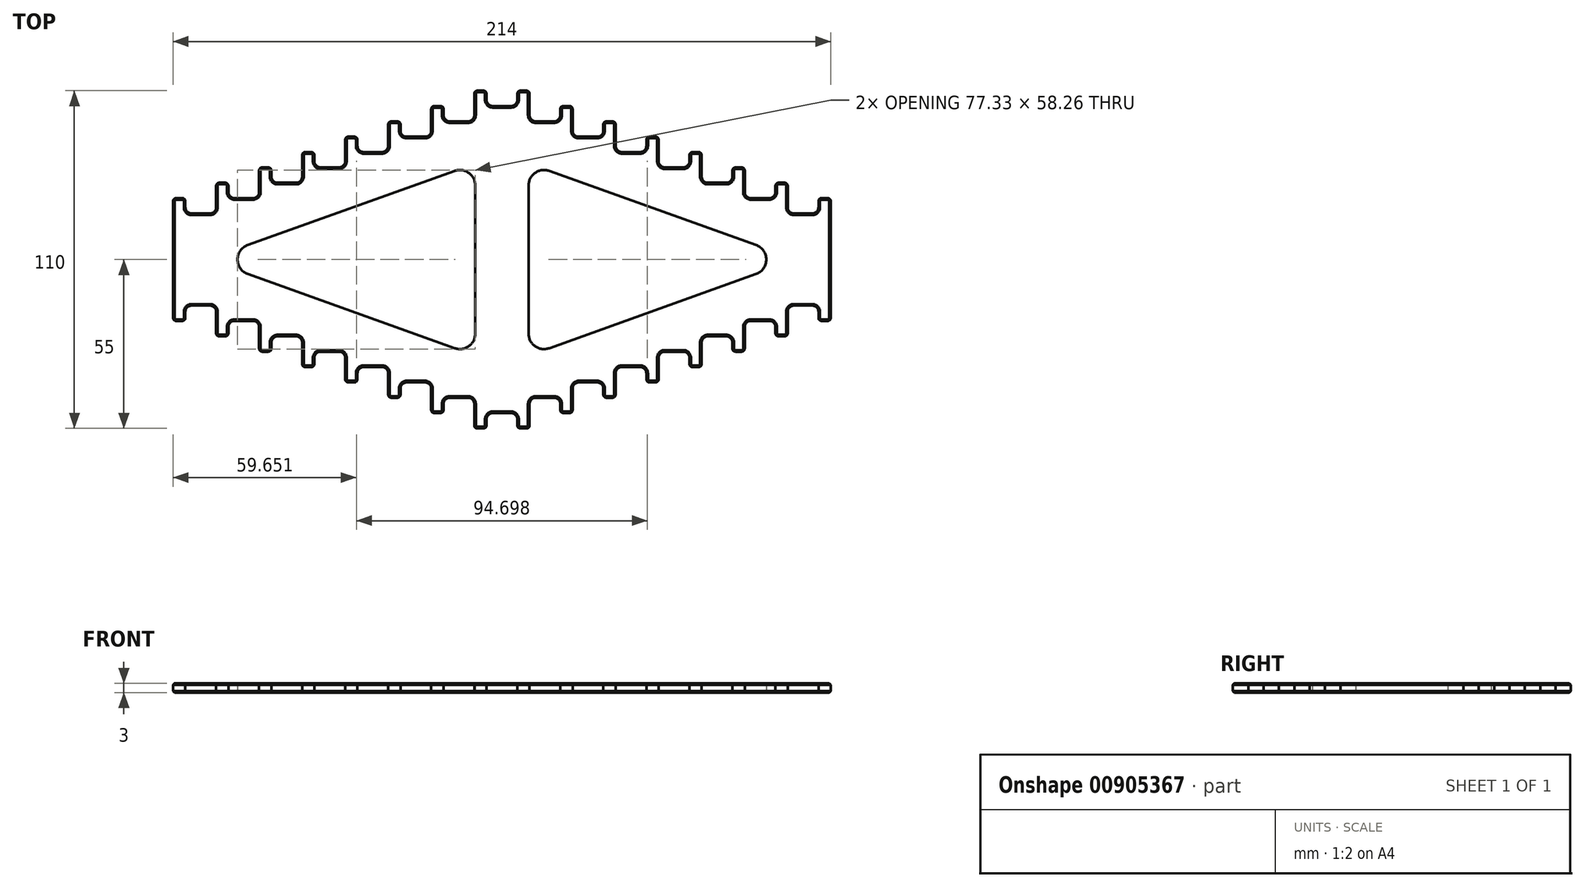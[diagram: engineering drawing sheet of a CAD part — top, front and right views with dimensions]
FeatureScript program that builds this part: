
annotation { "Feature Type Name" : "Feature", "Feature Type Description" : "" }
export const myFeature = defineFeature(function(context is Context, id is Id, definition is map)
    precondition{}
    {
        {
            var Q0;
            Q0=qCreatedBy(makeId("Top.planeOp"),FACE);
            var sketch = newSketch(context, id + "F0", { "sketchPlane" : qUnion([Q0])});
            skLineSegment(sketch, "E0", {"start": v(0, 0) * mm, "end": v(0, 34.38) * mm, "construction": true});
            skLineSegment(sketch, "E1", {"start": v(0, 0) * mm, "end": v(-95.82, 0) * mm, "construction": true});
            skLineSegment(sketch, "E2", {"start": v(0, 50) * mm, "end": v(-5, 50) * mm});
            skLineSegment(sketch, "E3", {"start": v(-5, 50) * mm, "end": v(-5, 55) * mm});
            skLineSegment(sketch, "E4", {"start": v(-5, 55) * mm, "end": v(-9, 55) * mm});
            skLineSegment(sketch, "E5", {"start": v(-9, 55) * mm, "end": v(-9, 45) * mm});
            skLineSegment(sketch, "E6", {"start": v(-9, 45) * mm, "end": v(-19, 45) * mm});
            skLineSegment(sketch, "E7", {"start": v(-19, 45) * mm, "end": v(-19, 50) * mm});
            skLineSegment(sketch, "E8", {"start": v(-19, 50) * mm, "end": v(-23, 50) * mm});
            skLineSegment(sketch, "E9", {"start": v(-23, 50) * mm, "end": v(-23, 40) * mm});
            skLineSegment(sketch, "E10", {"start": v(-23, 40) * mm, "end": v(-33, 40) * mm});
            skLineSegment(sketch, "E11", {"start": v(-33, 40) * mm, "end": v(-33, 45) * mm});
            skLineSegment(sketch, "E12", {"start": v(-33, 45) * mm, "end": v(-37, 45) * mm});
            skLineSegment(sketch, "E13", {"start": v(-37, 45) * mm, "end": v(-37, 35) * mm});
            skLineSegment(sketch, "E14", {"start": v(-37, 35) * mm, "end": v(-47, 35) * mm});
            skLineSegment(sketch, "E15", {"start": v(-47, 35) * mm, "end": v(-47, 40) * mm});
            skLineSegment(sketch, "E16", {"start": v(-47, 40) * mm, "end": v(-51, 40) * mm});
            skLineSegment(sketch, "E17", {"start": v(-51, 40) * mm, "end": v(-51, 30) * mm});
            skLineSegment(sketch, "E18", {"start": v(-51, 30) * mm, "end": v(-61, 30) * mm});
            skLineSegment(sketch, "E19", {"start": v(-61, 30) * mm, "end": v(-61, 35) * mm});
            skLineSegment(sketch, "E20", {"start": v(-61, 35) * mm, "end": v(-65, 35) * mm});
            skLineSegment(sketch, "E21", {"start": v(-65, 35) * mm, "end": v(-65, 25) * mm});
            skLineSegment(sketch, "E22", {"start": v(-65, 25) * mm, "end": v(-75, 25) * mm});
            skLineSegment(sketch, "E23", {"start": v(-75, 25) * mm, "end": v(-75, 30) * mm});
            skLineSegment(sketch, "E24", {"start": v(-75, 30) * mm, "end": v(-79, 30) * mm});
            skLineSegment(sketch, "E25", {"start": v(-79, 30) * mm, "end": v(-79, 20) * mm});
            skLineSegment(sketch, "E26", {"start": v(-79, 20) * mm, "end": v(-89, 20) * mm});
            skLineSegment(sketch, "E27", {"start": v(-89, 20) * mm, "end": v(-89, 25) * mm});
            skLineSegment(sketch, "E28", {"start": v(-89, 25) * mm, "end": v(-93, 25) * mm});
            skLineSegment(sketch, "E29", {"start": v(-93, 25) * mm, "end": v(-93, 15) * mm});
            skLineSegment(sketch, "E30", {"start": v(-93, 15) * mm, "end": v(-103, 15) * mm});
            skLineSegment(sketch, "E31", {"start": v(-103, 15) * mm, "end": v(-103, 20) * mm});
            skLineSegment(sketch, "E32", {"start": v(-103, 20) * mm, "end": v(-107, 20) * mm});
            skLineSegment(sketch, "E33", {"start": v(-107, 20) * mm, "end": v(-107, 0) * mm});
            skLineSegment(sketch, "E34.MirrorCS", {"start": v(47, 40) * mm, "end": v(51, 40) * mm});
            skLineSegment(sketch, "E35.MirrorCS", {"start": v(75, 30) * mm, "end": v(79, 30) * mm});
            skLineSegment(sketch, "E36.MirrorCS", {"start": v(61, 35) * mm, "end": v(65, 35) * mm});
            skLineSegment(sketch, "E37.MirrorCS", {"start": v(33, 45) * mm, "end": v(37, 45) * mm});
            skLineSegment(sketch, "E38.MirrorCS", {"start": v(89, 20) * mm, "end": v(89, 25) * mm});
            skLineSegment(sketch, "E39.MirrorCS", {"start": v(51, 30) * mm, "end": v(61, 30) * mm});
            skLineSegment(sketch, "E40.MirrorCS", {"start": v(37, 45) * mm, "end": v(37, 35) * mm});
            skLineSegment(sketch, "E41.MirrorCS", {"start": v(19, 45) * mm, "end": v(19, 50) * mm});
            skLineSegment(sketch, "E42.MirrorCS", {"start": v(65, 25) * mm, "end": v(75, 25) * mm});
            skLineSegment(sketch, "E43.MirrorCS", {"start": v(9, 45) * mm, "end": v(19, 45) * mm});
            skLineSegment(sketch, "E44.MirrorCS", {"start": v(79, 30) * mm, "end": v(79, 20) * mm});
            skLineSegment(sketch, "E45.MirrorCS", {"start": v(75, 25) * mm, "end": v(75, 30) * mm});
            skLineSegment(sketch, "E46.MirrorCS", {"start": v(65, 35) * mm, "end": v(65, 25) * mm});
            skLineSegment(sketch, "E47.MirrorCS", {"start": v(5, 50) * mm, "end": v(5, 55) * mm});
            skLineSegment(sketch, "E48.MirrorCS", {"start": v(47, 35) * mm, "end": v(47, 40) * mm});
            skLineSegment(sketch, "E49.MirrorCS", {"start": v(61, 30) * mm, "end": v(61, 35) * mm});
            skLineSegment(sketch, "E50.MirrorCS", {"start": v(103, 20) * mm, "end": v(107, 20) * mm});
            skLineSegment(sketch, "E51.MirrorCS", {"start": v(79, 20) * mm, "end": v(89, 20) * mm});
            skLineSegment(sketch, "E52.MirrorCS", {"start": v(89, 25) * mm, "end": v(93, 25) * mm});
            skLineSegment(sketch, "E53.MirrorCS", {"start": v(103, 15) * mm, "end": v(103, 20) * mm});
            skLineSegment(sketch, "E54.MirrorCS", {"start": v(9, 55) * mm, "end": v(9, 45) * mm});
            skLineSegment(sketch, "E55.MirrorCS", {"start": v(37, 35) * mm, "end": v(47, 35) * mm});
            skLineSegment(sketch, "E56.MirrorCS", {"start": v(51, 40) * mm, "end": v(51, 30) * mm});
            skLineSegment(sketch, "E57.MirrorCS", {"start": v(93, 25) * mm, "end": v(93, 15) * mm});
            skLineSegment(sketch, "E58.MirrorCS", {"start": v(33, 40) * mm, "end": v(33, 45) * mm});
            skLineSegment(sketch, "E59.MirrorCS", {"start": v(23, 50) * mm, "end": v(23, 40) * mm});
            skLineSegment(sketch, "E60.MirrorCS", {"start": v(93, 15) * mm, "end": v(103, 15) * mm});
            skLineSegment(sketch, "E61.MirrorCS", {"start": v(19, 50) * mm, "end": v(23, 50) * mm});
            skLineSegment(sketch, "E62.MirrorCS", {"start": v(23, 40) * mm, "end": v(33, 40) * mm});
            skLineSegment(sketch, "E63.MirrorCS", {"start": v(5, 55) * mm, "end": v(9, 55) * mm});
            skLineSegment(sketch, "E64.MirrorCS", {"start": v(107, 20) * mm, "end": v(107, 0) * mm});
            skLineSegment(sketch, "E65.MirrorCS", {"start": v(-33, -45) * mm, "end": v(-37, -45) * mm});
            skLineSegment(sketch, "E66.MirrorCS", {"start": v(-33, -40) * mm, "end": v(-33, -45) * mm});
            skLineSegment(sketch, "E67.MirrorCS", {"start": v(33, -40) * mm, "end": v(33, -45) * mm});
            skLineSegment(sketch, "E68.MirrorCS", {"start": v(-61, -30) * mm, "end": v(-61, -35) * mm});
            skLineSegment(sketch, "E69.MirrorCS", {"start": v(-47, -35) * mm, "end": v(-47, -40) * mm});
            skLineSegment(sketch, "E70.MirrorCS", {"start": v(5, -55) * mm, "end": v(9, -55) * mm});
            skLineSegment(sketch, "E71.MirrorCS", {"start": v(-75, -30) * mm, "end": v(-79, -30) * mm});
            skLineSegment(sketch, "E72.MirrorCS", {"start": v(-89, -20) * mm, "end": v(-89, -25) * mm});
            skLineSegment(sketch, "E73.MirrorCS", {"start": v(103, -15) * mm, "end": v(103, -20) * mm});
            skLineSegment(sketch, "E74.MirrorCS", {"start": v(-19, -45) * mm, "end": v(-19, -50) * mm});
            skLineSegment(sketch, "E75.MirrorCS", {"start": v(-103, -20) * mm, "end": v(-107, -20) * mm});
            skLineSegment(sketch, "E76.MirrorCS", {"start": v(75, -30) * mm, "end": v(79, -30) * mm});
            skLineSegment(sketch, "E77.MirrorCS", {"start": v(-89, -25) * mm, "end": v(-93, -25) * mm});
            skLineSegment(sketch, "E78.MirrorCS", {"start": v(-47, -40) * mm, "end": v(-51, -40) * mm});
            skLineSegment(sketch, "E79.MirrorCS", {"start": v(89, -20) * mm, "end": v(89, -25) * mm});
            skLineSegment(sketch, "E80.MirrorCS", {"start": v(103, -20) * mm, "end": v(107, -20) * mm});
            skLineSegment(sketch, "E81.MirrorCS", {"start": v(19, -45) * mm, "end": v(19, -50) * mm});
            skLineSegment(sketch, "E82.MirrorCS", {"start": v(61, -30) * mm, "end": v(61, -35) * mm});
            skLineSegment(sketch, "E83.MirrorCS", {"start": v(-103, -15) * mm, "end": v(-103, -20) * mm});
            skLineSegment(sketch, "E84.MirrorCS", {"start": v(-5, -50) * mm, "end": v(-5, -55) * mm});
            skLineSegment(sketch, "E85.MirrorCS", {"start": v(47, -40) * mm, "end": v(51, -40) * mm});
            skLineSegment(sketch, "E86.MirrorCS", {"start": v(19, -50) * mm, "end": v(23, -50) * mm});
            skLineSegment(sketch, "E87.MirrorCS", {"start": v(-5, -55) * mm, "end": v(-9, -55) * mm});
            skLineSegment(sketch, "E88.MirrorCS", {"start": v(-61, -35) * mm, "end": v(-65, -35) * mm});
            skLineSegment(sketch, "E89.MirrorCS", {"start": v(89, -25) * mm, "end": v(93, -25) * mm});
            skLineSegment(sketch, "E90.MirrorCS", {"start": v(33, -45) * mm, "end": v(37, -45) * mm});
            skLineSegment(sketch, "E91.MirrorCS", {"start": v(47, -35) * mm, "end": v(47, -40) * mm});
            skLineSegment(sketch, "E92.MirrorCS", {"start": v(75, -25) * mm, "end": v(75, -30) * mm});
            skLineSegment(sketch, "E93.MirrorCS", {"start": v(-19, -50) * mm, "end": v(-23, -50) * mm});
            skLineSegment(sketch, "E94.MirrorCS", {"start": v(61, -35) * mm, "end": v(65, -35) * mm});
            skLineSegment(sketch, "E95.MirrorCS", {"start": v(-75, -25) * mm, "end": v(-75, -30) * mm});
            skLineSegment(sketch, "E96.MirrorCS", {"start": v(0, -50) * mm, "end": v(-5, -50) * mm});
            skLineSegment(sketch, "E97.MirrorCS", {"start": v(5, -50) * mm, "end": v(5, -55) * mm});
            skLineSegment(sketch, "E98.MirrorCS", {"start": v(65, -35) * mm, "end": v(65, -25) * mm});
            skLineSegment(sketch, "E99.MirrorCS", {"start": v(-93, -15) * mm, "end": v(-103, -15) * mm});
            skLineSegment(sketch, "E100.MirrorCS", {"start": v(-37, -45) * mm, "end": v(-37, -35) * mm});
            skLineSegment(sketch, "E101.MirrorCS", {"start": v(-93, -25) * mm, "end": v(-93, -15) * mm});
            skLineSegment(sketch, "E102.MirrorCS", {"start": v(-51, -30) * mm, "end": v(-61, -30) * mm});
            skLineSegment(sketch, "E103.MirrorCS", {"start": v(79, -20) * mm, "end": v(89, -20) * mm});
            skLineSegment(sketch, "E104.MirrorCS", {"start": v(-51, -40) * mm, "end": v(-51, -30) * mm});
            skLineSegment(sketch, "E105.MirrorCS", {"start": v(-23, -40) * mm, "end": v(-33, -40) * mm});
            skLineSegment(sketch, "E106.MirrorCS", {"start": v(37, -35) * mm, "end": v(47, -35) * mm});
            skLineSegment(sketch, "E107.MirrorCS", {"start": v(79, -30) * mm, "end": v(79, -20) * mm});
            skLineSegment(sketch, "E108.MirrorCS", {"start": v(-9, -45) * mm, "end": v(-19, -45) * mm});
            skLineSegment(sketch, "E109.MirrorCS", {"start": v(51, -30) * mm, "end": v(61, -30) * mm});
            skLineSegment(sketch, "E110.MirrorCS", {"start": v(-65, -35) * mm, "end": v(-65, -25) * mm});
            skLineSegment(sketch, "E111.MirrorCS", {"start": v(-23, -50) * mm, "end": v(-23, -40) * mm});
            skLineSegment(sketch, "E112.MirrorCS", {"start": v(93, -25) * mm, "end": v(93, -15) * mm});
            skLineSegment(sketch, "E113.MirrorCS", {"start": v(9, -45) * mm, "end": v(19, -45) * mm});
            skLineSegment(sketch, "E114.MirrorCS", {"start": v(-9, -55) * mm, "end": v(-9, -45) * mm});
            skLineSegment(sketch, "E115.MirrorCS", {"start": v(23, -40) * mm, "end": v(33, -40) * mm});
            skLineSegment(sketch, "E116.MirrorCS", {"start": v(-79, -30) * mm, "end": v(-79, -20) * mm});
            skLineSegment(sketch, "E117.MirrorCS", {"start": v(9, -55) * mm, "end": v(9, -45) * mm});
            skLineSegment(sketch, "E118.MirrorCS", {"start": v(-79, -20) * mm, "end": v(-89, -20) * mm});
            skLineSegment(sketch, "E119.MirrorCS", {"start": v(23, -50) * mm, "end": v(23, -40) * mm});
            skLineSegment(sketch, "E120.MirrorCS", {"start": v(51, -40) * mm, "end": v(51, -30) * mm});
            skLineSegment(sketch, "E121.MirrorCS", {"start": v(37, -45) * mm, "end": v(37, -35) * mm});
            skLineSegment(sketch, "E122.MirrorCS", {"start": v(-65, -25) * mm, "end": v(-75, -25) * mm});
            skLineSegment(sketch, "E123.MirrorCS", {"start": v(-37, -35) * mm, "end": v(-47, -35) * mm});
            skLineSegment(sketch, "E124.MirrorCS", {"start": v(93, -15) * mm, "end": v(103, -15) * mm});
            skLineSegment(sketch, "E125.MirrorCS", {"start": v(65, -25) * mm, "end": v(75, -25) * mm});
            skLineSegment(sketch, "E126.MirrorCS", {"start": v(107, -20) * mm, "end": v(107, 0) * mm});
            skLineSegment(sketch, "E127.MirrorCS", {"start": v(-107, -20) * mm, "end": v(-107, 0) * mm});
            skLineSegment(sketch, "E128", {"start": v(5, 50) * mm, "end": v(0, 50) * mm});
            skLineSegment(sketch, "E129", {"start": v(5, -50) * mm, "end": v(0, -50) * mm});
            skLineSegment(sketch, "E130.MirrorCS", {"start": v(0, 0) * mm, "end": v(0, -34.38) * mm, "construction": true});
            skLineSegment(sketch, "E131.MirrorCS", {"start": v(0, 0) * mm, "end": v(95.82, 0) * mm, "construction": true});
            skLineSegment(sketch, "E132", {"start": v(-95.82, 0) * mm, "end": v(0, 34.38) * mm});
            skLineSegment(sketch, "E133.MirrorCS", {"start": v(95.82, 0) * mm, "end": v(0, 34.38) * mm});
            skLineSegment(sketch, "E134.MirrorCS", {"start": v(-95.82, 0) * mm, "end": v(0, -34.38) * mm});
            skLineSegment(sketch, "E135.MirrorCS", {"start": v(95.82, 0) * mm, "end": v(0, -34.38) * mm});
            skLineSegment(sketch, "E136", {"start": v(-8.68, 31.26) * mm, "end": v(-8.68, -31.26) * mm});
            skLineSegment(sketch, "E137.MirrorCS", {"start": v(8.68, 31.26) * mm, "end": v(8.68, -31.26) * mm});
            skSolve(sketch);
        }
        {
            var Q0;
            Q0=makeQuery(id+"F0.imprint","IMPRINT",FACE,{"disambiguationData":[TD([[makeQuery(id+"F0.imprint","IMPRINT",EDGE,{"derivedFrom":sQuery(id+"F0.wireOp",EDGE,"E2")}),1.0]])]});
            var Q1;
            {var subQ4=sQuery(id+"F0.wireOp",EDGE,"E136");Q1=makeQuery(id+"F0.imprint","IMPRINT",FACE,{"disambiguationData":[TD([[makeQuery(id+"F0.imprint","IMPRINT",EDGE,{"derivedFrom":subQ4}),1.0]])]});}
            extrude(context, id + "F1", {"entities" : qUnion([Q0, Q1]), "depth" : 3 * mm, "offsetDistance" : 25 * mm});
        }
        {
            var Q0;
            Q0=makeQuery(id+"F1.opExtrude","SWEPT_EDGE",EDGE,{"disambiguationData":[OSD([sQuery(id+"F0.wireOp",EDGE,"E30"),sQuery(id+"F0.wireOp",EDGE,"E31")])]});
            var Q1;
            Q1=makeQuery(id+"F1.opExtrude","SWEPT_EDGE",EDGE,{"disambiguationData":[OSD([sQuery(id+"F0.wireOp",EDGE,"E26"),sQuery(id+"F0.wireOp",EDGE,"E27")])]});
            var Q2;
            Q2=makeQuery(id+"F1.opExtrude","SWEPT_EDGE",EDGE,{"disambiguationData":[OSD([sQuery(id+"F0.wireOp",EDGE,"E22"),sQuery(id+"F0.wireOp",EDGE,"E23")])]});
            var Q3;
            Q3=makeQuery(id+"F1.opExtrude","SWEPT_EDGE",EDGE,{"disambiguationData":[OSD([sQuery(id+"F0.wireOp",EDGE,"E18"),sQuery(id+"F0.wireOp",EDGE,"E19")])]});
            var Q4;
            Q4=makeQuery(id+"F1.opExtrude","SWEPT_EDGE",EDGE,{"disambiguationData":[OSD([sQuery(id+"F0.wireOp",EDGE,"E14"),sQuery(id+"F0.wireOp",EDGE,"E15")])]});
            var Q5;
            Q5=makeQuery(id+"F1.opExtrude","SWEPT_EDGE",EDGE,{"disambiguationData":[OSD([sQuery(id+"F0.wireOp",EDGE,"E10"),sQuery(id+"F0.wireOp",EDGE,"E11")])]});
            var Q6;
            Q6=makeQuery(id+"F1.opExtrude","SWEPT_EDGE",EDGE,{"disambiguationData":[OSD([sQuery(id+"F0.wireOp",EDGE,"E6"),sQuery(id+"F0.wireOp",EDGE,"E7")])]});
            var Q7;
            Q7=makeQuery(id+"F1.opExtrude","SWEPT_EDGE",EDGE,{"disambiguationData":[OSD([sQuery(id+"F0.wireOp",EDGE,"E2"),sQuery(id+"F0.wireOp",EDGE,"E3")])]});
            var Q8;
            Q8=makeQuery(id+"F1.opExtrude","SWEPT_EDGE",EDGE,{"disambiguationData":[OSD([sQuery(id+"F0.wireOp",EDGE,"E29"),sQuery(id+"F0.wireOp",EDGE,"E30")])]});
            var Q9;
            Q9=makeQuery(id+"F1.opExtrude","SWEPT_EDGE",EDGE,{"disambiguationData":[OSD([sQuery(id+"F0.wireOp",EDGE,"E25"),sQuery(id+"F0.wireOp",EDGE,"E26")])]});
            var Q10;
            Q10=makeQuery(id+"F1.opExtrude","SWEPT_EDGE",EDGE,{"disambiguationData":[OSD([sQuery(id+"F0.wireOp",EDGE,"E21"),sQuery(id+"F0.wireOp",EDGE,"E22")])]});
            var Q11;
            Q11=makeQuery(id+"F1.opExtrude","SWEPT_EDGE",EDGE,{"disambiguationData":[OSD([sQuery(id+"F0.wireOp",EDGE,"E17"),sQuery(id+"F0.wireOp",EDGE,"E18")])]});
            var Q12;
            Q12=makeQuery(id+"F1.opExtrude","SWEPT_EDGE",EDGE,{"disambiguationData":[OSD([sQuery(id+"F0.wireOp",EDGE,"E13"),sQuery(id+"F0.wireOp",EDGE,"E14")])]});
            var Q13;
            Q13=makeQuery(id+"F1.opExtrude","SWEPT_EDGE",EDGE,{"disambiguationData":[OSD([sQuery(id+"F0.wireOp",EDGE,"E9"),sQuery(id+"F0.wireOp",EDGE,"E10")])]});
            var Q14;
            Q14=makeQuery(id+"F1.opExtrude","SWEPT_EDGE",EDGE,{"disambiguationData":[OSD([sQuery(id+"F0.wireOp",EDGE,"E5"),sQuery(id+"F0.wireOp",EDGE,"E6")])]});
            var Q15;
            Q15=makeQuery(id+"F1.opExtrude","SWEPT_EDGE",EDGE,{"disambiguationData":[OSD([sQuery(id+"F0.wireOp",EDGE,"E47.MirrorCS"),sQuery(id+"F0.wireOp",EDGE,"E128")])]});
            var Q16;
            Q16=makeQuery(id+"F1.opExtrude","SWEPT_EDGE",EDGE,{"disambiguationData":[OSD([sQuery(id+"F0.wireOp",EDGE,"E41.MirrorCS"),sQuery(id+"F0.wireOp",EDGE,"E43.MirrorCS")])]});
            var Q17;
            Q17=makeQuery(id+"F1.opExtrude","SWEPT_EDGE",EDGE,{"disambiguationData":[OSD([sQuery(id+"F0.wireOp",EDGE,"E58.MirrorCS"),sQuery(id+"F0.wireOp",EDGE,"E62.MirrorCS")])]});
            var Q18;
            Q18=makeQuery(id+"F1.opExtrude","SWEPT_EDGE",EDGE,{"disambiguationData":[OSD([sQuery(id+"F0.wireOp",EDGE,"E48.MirrorCS"),sQuery(id+"F0.wireOp",EDGE,"E55.MirrorCS")])]});
            var Q19;
            Q19=makeQuery(id+"F1.opExtrude","SWEPT_EDGE",EDGE,{"disambiguationData":[OSD([sQuery(id+"F0.wireOp",EDGE,"E39.MirrorCS"),sQuery(id+"F0.wireOp",EDGE,"E49.MirrorCS")])]});
            var Q20;
            Q20=makeQuery(id+"F1.opExtrude","SWEPT_EDGE",EDGE,{"disambiguationData":[OSD([sQuery(id+"F0.wireOp",EDGE,"E42.MirrorCS"),sQuery(id+"F0.wireOp",EDGE,"E45.MirrorCS")])]});
            var Q21;
            Q21=makeQuery(id+"F1.opExtrude","SWEPT_EDGE",EDGE,{"disambiguationData":[OSD([sQuery(id+"F0.wireOp",EDGE,"E38.MirrorCS"),sQuery(id+"F0.wireOp",EDGE,"E51.MirrorCS")])]});
            var Q22;
            Q22=makeQuery(id+"F1.opExtrude","SWEPT_EDGE",EDGE,{"disambiguationData":[OSD([sQuery(id+"F0.wireOp",EDGE,"E53.MirrorCS"),sQuery(id+"F0.wireOp",EDGE,"E60.MirrorCS")])]});
            var Q23;
            Q23=makeQuery(id+"F1.opExtrude","SWEPT_EDGE",EDGE,{"disambiguationData":[OSD([sQuery(id+"F0.wireOp",EDGE,"E43.MirrorCS"),sQuery(id+"F0.wireOp",EDGE,"E54.MirrorCS")])]});
            var Q24;
            Q24=makeQuery(id+"F1.opExtrude","SWEPT_EDGE",EDGE,{"disambiguationData":[OSD([sQuery(id+"F0.wireOp",EDGE,"E59.MirrorCS"),sQuery(id+"F0.wireOp",EDGE,"E62.MirrorCS")])]});
            var Q25;
            Q25=makeQuery(id+"F1.opExtrude","SWEPT_EDGE",EDGE,{"disambiguationData":[OSD([sQuery(id+"F0.wireOp",EDGE,"E40.MirrorCS"),sQuery(id+"F0.wireOp",EDGE,"E55.MirrorCS")])]});
            var Q26;
            Q26=makeQuery(id+"F1.opExtrude","SWEPT_EDGE",EDGE,{"disambiguationData":[OSD([sQuery(id+"F0.wireOp",EDGE,"E39.MirrorCS"),sQuery(id+"F0.wireOp",EDGE,"E56.MirrorCS")])]});
            var Q27;
            Q27=makeQuery(id+"F1.opExtrude","SWEPT_EDGE",EDGE,{"disambiguationData":[OSD([sQuery(id+"F0.wireOp",EDGE,"E42.MirrorCS"),sQuery(id+"F0.wireOp",EDGE,"E46.MirrorCS")])]});
            var Q28;
            Q28=makeQuery(id+"F1.opExtrude","SWEPT_EDGE",EDGE,{"disambiguationData":[OSD([sQuery(id+"F0.wireOp",EDGE,"E44.MirrorCS"),sQuery(id+"F0.wireOp",EDGE,"E51.MirrorCS")])]});
            var Q29;
            Q29=makeQuery(id+"F1.opExtrude","SWEPT_EDGE",EDGE,{"disambiguationData":[OSD([sQuery(id+"F0.wireOp",EDGE,"E57.MirrorCS"),sQuery(id+"F0.wireOp",EDGE,"E60.MirrorCS")])]});
            var Q30;
            Q30=makeQuery(id+"F1.opExtrude","SWEPT_EDGE",EDGE,{"disambiguationData":[OSD([sQuery(id+"F0.wireOp",EDGE,"E112.MirrorCS"),sQuery(id+"F0.wireOp",EDGE,"E124.MirrorCS")])]});
            var Q31;
            Q31=makeQuery(id+"F1.opExtrude","SWEPT_EDGE",EDGE,{"disambiguationData":[OSD([sQuery(id+"F0.wireOp",EDGE,"E103.MirrorCS"),sQuery(id+"F0.wireOp",EDGE,"E107.MirrorCS")])]});
            var Q32;
            Q32=makeQuery(id+"F1.opExtrude","SWEPT_EDGE",EDGE,{"disambiguationData":[OSD([sQuery(id+"F0.wireOp",EDGE,"E98.MirrorCS"),sQuery(id+"F0.wireOp",EDGE,"E125.MirrorCS")])]});
            var Q33;
            Q33=makeQuery(id+"F1.opExtrude","SWEPT_EDGE",EDGE,{"disambiguationData":[OSD([sQuery(id+"F0.wireOp",EDGE,"E109.MirrorCS"),sQuery(id+"F0.wireOp",EDGE,"E120.MirrorCS")])]});
            var Q34;
            Q34=makeQuery(id+"F1.opExtrude","SWEPT_EDGE",EDGE,{"disambiguationData":[OSD([sQuery(id+"F0.wireOp",EDGE,"E106.MirrorCS"),sQuery(id+"F0.wireOp",EDGE,"E121.MirrorCS")])]});
            var Q35;
            Q35=makeQuery(id+"F1.opExtrude","SWEPT_EDGE",EDGE,{"disambiguationData":[OSD([sQuery(id+"F0.wireOp",EDGE,"E115.MirrorCS"),sQuery(id+"F0.wireOp",EDGE,"E119.MirrorCS")])]});
            var Q36;
            Q36=makeQuery(id+"F1.opExtrude","SWEPT_EDGE",EDGE,{"disambiguationData":[OSD([sQuery(id+"F0.wireOp",EDGE,"E113.MirrorCS"),sQuery(id+"F0.wireOp",EDGE,"E117.MirrorCS")])]});
            var Q37;
            Q37=makeQuery(id+"F1.opExtrude","SWEPT_EDGE",EDGE,{"disambiguationData":[OSD([sQuery(id+"F0.wireOp",EDGE,"E84.MirrorCS"),sQuery(id+"F0.wireOp",EDGE,"E96.MirrorCS")])]});
            var Q38;
            Q38=makeQuery(id+"F1.opExtrude","SWEPT_EDGE",EDGE,{"disambiguationData":[OSD([sQuery(id+"F0.wireOp",EDGE,"E74.MirrorCS"),sQuery(id+"F0.wireOp",EDGE,"E108.MirrorCS")])]});
            var Q39;
            Q39=makeQuery(id+"F1.opExtrude","SWEPT_EDGE",EDGE,{"disambiguationData":[OSD([sQuery(id+"F0.wireOp",EDGE,"E66.MirrorCS"),sQuery(id+"F0.wireOp",EDGE,"E105.MirrorCS")])]});
            var Q40;
            Q40=makeQuery(id+"F1.opExtrude","SWEPT_EDGE",EDGE,{"disambiguationData":[OSD([sQuery(id+"F0.wireOp",EDGE,"E69.MirrorCS"),sQuery(id+"F0.wireOp",EDGE,"E123.MirrorCS")])]});
            var Q41;
            Q41=makeQuery(id+"F1.opExtrude","SWEPT_EDGE",EDGE,{"disambiguationData":[OSD([sQuery(id+"F0.wireOp",EDGE,"E68.MirrorCS"),sQuery(id+"F0.wireOp",EDGE,"E102.MirrorCS")])]});
            var Q42;
            Q42=makeQuery(id+"F1.opExtrude","SWEPT_EDGE",EDGE,{"disambiguationData":[OSD([sQuery(id+"F0.wireOp",EDGE,"E95.MirrorCS"),sQuery(id+"F0.wireOp",EDGE,"E122.MirrorCS")])]});
            var Q43;
            Q43=makeQuery(id+"F1.opExtrude","SWEPT_EDGE",EDGE,{"disambiguationData":[OSD([sQuery(id+"F0.wireOp",EDGE,"E72.MirrorCS"),sQuery(id+"F0.wireOp",EDGE,"E118.MirrorCS")])]});
            var Q44;
            Q44=makeQuery(id+"F1.opExtrude","SWEPT_EDGE",EDGE,{"disambiguationData":[OSD([sQuery(id+"F0.wireOp",EDGE,"E83.MirrorCS"),sQuery(id+"F0.wireOp",EDGE,"E99.MirrorCS")])]});
            var Q45;
            Q45=makeQuery(id+"F1.opExtrude","SWEPT_EDGE",EDGE,{"disambiguationData":[OSD([sQuery(id+"F0.wireOp",EDGE,"E99.MirrorCS"),sQuery(id+"F0.wireOp",EDGE,"E101.MirrorCS")])]});
            var Q46;
            Q46=makeQuery(id+"F1.opExtrude","SWEPT_EDGE",EDGE,{"disambiguationData":[OSD([sQuery(id+"F0.wireOp",EDGE,"E116.MirrorCS"),sQuery(id+"F0.wireOp",EDGE,"E118.MirrorCS")])]});
            var Q47;
            Q47=makeQuery(id+"F1.opExtrude","SWEPT_EDGE",EDGE,{"disambiguationData":[OSD([sQuery(id+"F0.wireOp",EDGE,"E110.MirrorCS"),sQuery(id+"F0.wireOp",EDGE,"E122.MirrorCS")])]});
            var Q48;
            Q48=makeQuery(id+"F1.opExtrude","SWEPT_EDGE",EDGE,{"disambiguationData":[OSD([sQuery(id+"F0.wireOp",EDGE,"E102.MirrorCS"),sQuery(id+"F0.wireOp",EDGE,"E104.MirrorCS")])]});
            var Q49;
            Q49=makeQuery(id+"F1.opExtrude","SWEPT_EDGE",EDGE,{"disambiguationData":[OSD([sQuery(id+"F0.wireOp",EDGE,"E100.MirrorCS"),sQuery(id+"F0.wireOp",EDGE,"E123.MirrorCS")])]});
            var Q50;
            Q50=makeQuery(id+"F1.opExtrude","SWEPT_EDGE",EDGE,{"disambiguationData":[OSD([sQuery(id+"F0.wireOp",EDGE,"E105.MirrorCS"),sQuery(id+"F0.wireOp",EDGE,"E111.MirrorCS")])]});
            var Q51;
            Q51=makeQuery(id+"F1.opExtrude","SWEPT_EDGE",EDGE,{"disambiguationData":[OSD([sQuery(id+"F0.wireOp",EDGE,"E108.MirrorCS"),sQuery(id+"F0.wireOp",EDGE,"E114.MirrorCS")])]});
            var Q52;
            Q52=makeQuery(id+"F1.opExtrude","SWEPT_EDGE",EDGE,{"disambiguationData":[OSD([sQuery(id+"F0.wireOp",EDGE,"E97.MirrorCS"),sQuery(id+"F0.wireOp",EDGE,"E129")])]});
            var Q53;
            Q53=makeQuery(id+"F1.opExtrude","SWEPT_EDGE",EDGE,{"disambiguationData":[OSD([sQuery(id+"F0.wireOp",EDGE,"E81.MirrorCS"),sQuery(id+"F0.wireOp",EDGE,"E113.MirrorCS")])]});
            var Q54;
            Q54=makeQuery(id+"F1.opExtrude","SWEPT_EDGE",EDGE,{"disambiguationData":[OSD([sQuery(id+"F0.wireOp",EDGE,"E67.MirrorCS"),sQuery(id+"F0.wireOp",EDGE,"E115.MirrorCS")])]});
            var Q55;
            Q55=makeQuery(id+"F1.opExtrude","SWEPT_EDGE",EDGE,{"disambiguationData":[OSD([sQuery(id+"F0.wireOp",EDGE,"E91.MirrorCS"),sQuery(id+"F0.wireOp",EDGE,"E106.MirrorCS")])]});
            var Q56;
            Q56=makeQuery(id+"F1.opExtrude","SWEPT_EDGE",EDGE,{"disambiguationData":[OSD([sQuery(id+"F0.wireOp",EDGE,"E82.MirrorCS"),sQuery(id+"F0.wireOp",EDGE,"E109.MirrorCS")])]});
            var Q57;
            Q57=makeQuery(id+"F1.opExtrude","SWEPT_EDGE",EDGE,{"disambiguationData":[OSD([sQuery(id+"F0.wireOp",EDGE,"E92.MirrorCS"),sQuery(id+"F0.wireOp",EDGE,"E125.MirrorCS")])]});
            var Q58;
            Q58=makeQuery(id+"F1.opExtrude","SWEPT_EDGE",EDGE,{"disambiguationData":[OSD([sQuery(id+"F0.wireOp",EDGE,"E79.MirrorCS"),sQuery(id+"F0.wireOp",EDGE,"E103.MirrorCS")])]});
            var Q59;
            Q59=makeQuery(id+"F1.opExtrude","SWEPT_EDGE",EDGE,{"disambiguationData":[OSD([sQuery(id+"F0.wireOp",EDGE,"E73.MirrorCS"),sQuery(id+"F0.wireOp",EDGE,"E124.MirrorCS")])]});
            fillet(context, id + "F2", {"entities" : qUnion([Q0, Q1, Q2, Q3, Q4, Q5, Q6, Q7, Q8, Q9, Q10, Q11, Q12, Q13, Q14, Q15, Q16, Q17, Q18, Q19, Q20, Q21, Q22, Q23, Q24, Q25, Q26, Q27, Q28, Q29, Q30, Q31, Q32, Q33, Q34, Q35, Q36, Q37, Q38, Q39, Q40, Q41, Q42, Q43, Q44, Q45, Q46, Q47, Q48, Q49, Q50, Q51, Q52, Q53, Q54, Q55, Q56, Q57, Q58, Q59]), "radius" : 2 * mm, "tangentPropagation" : true, "allowEdgeOverflow" : false});
        }
        {
            var Q0;
            Q0=makeQuery(id+"F1.opExtrude","SWEPT_EDGE",EDGE,{"disambiguationData":[OSD([sQuery(id+"F0.wireOp",EDGE,"E32"),sQuery(id+"F0.wireOp",EDGE,"E33")])]});
            var Q1;
            Q1=makeQuery(id+"F1.opExtrude","SWEPT_EDGE",EDGE,{"disambiguationData":[OSD([sQuery(id+"F0.wireOp",EDGE,"E28"),sQuery(id+"F0.wireOp",EDGE,"E29")])]});
            var Q2;
            Q2=makeQuery(id+"F1.opExtrude","SWEPT_EDGE",EDGE,{"disambiguationData":[OSD([sQuery(id+"F0.wireOp",EDGE,"E24"),sQuery(id+"F0.wireOp",EDGE,"E25")])]});
            var Q3;
            Q3=makeQuery(id+"F1.opExtrude","SWEPT_EDGE",EDGE,{"disambiguationData":[OSD([sQuery(id+"F0.wireOp",EDGE,"E20"),sQuery(id+"F0.wireOp",EDGE,"E21")])]});
            var Q4;
            Q4=makeQuery(id+"F1.opExtrude","SWEPT_EDGE",EDGE,{"disambiguationData":[OSD([sQuery(id+"F0.wireOp",EDGE,"E16"),sQuery(id+"F0.wireOp",EDGE,"E17")])]});
            var Q5;
            Q5=makeQuery(id+"F1.opExtrude","SWEPT_EDGE",EDGE,{"disambiguationData":[OSD([sQuery(id+"F0.wireOp",EDGE,"E12"),sQuery(id+"F0.wireOp",EDGE,"E13")])]});
            var Q6;
            Q6=makeQuery(id+"F1.opExtrude","SWEPT_EDGE",EDGE,{"disambiguationData":[OSD([sQuery(id+"F0.wireOp",EDGE,"E8"),sQuery(id+"F0.wireOp",EDGE,"E9")])]});
            var Q7;
            Q7=makeQuery(id+"F1.opExtrude","SWEPT_EDGE",EDGE,{"disambiguationData":[OSD([sQuery(id+"F0.wireOp",EDGE,"E4"),sQuery(id+"F0.wireOp",EDGE,"E5")])]});
            var Q8;
            Q8=makeQuery(id+"F1.opExtrude","SWEPT_EDGE",EDGE,{"disambiguationData":[OSD([sQuery(id+"F0.wireOp",EDGE,"E47.MirrorCS"),sQuery(id+"F0.wireOp",EDGE,"E63.MirrorCS")])]});
            var Q9;
            Q9=makeQuery(id+"F1.opExtrude","SWEPT_EDGE",EDGE,{"disambiguationData":[OSD([sQuery(id+"F0.wireOp",EDGE,"E41.MirrorCS"),sQuery(id+"F0.wireOp",EDGE,"E61.MirrorCS")])]});
            var Q10;
            Q10=makeQuery(id+"F1.opExtrude","SWEPT_EDGE",EDGE,{"disambiguationData":[OSD([sQuery(id+"F0.wireOp",EDGE,"E37.MirrorCS"),sQuery(id+"F0.wireOp",EDGE,"E58.MirrorCS")])]});
            var Q11;
            Q11=makeQuery(id+"F1.opExtrude","SWEPT_EDGE",EDGE,{"disambiguationData":[OSD([sQuery(id+"F0.wireOp",EDGE,"E34.MirrorCS"),sQuery(id+"F0.wireOp",EDGE,"E48.MirrorCS")])]});
            var Q12;
            Q12=makeQuery(id+"F1.opExtrude","SWEPT_EDGE",EDGE,{"disambiguationData":[OSD([sQuery(id+"F0.wireOp",EDGE,"E36.MirrorCS"),sQuery(id+"F0.wireOp",EDGE,"E49.MirrorCS")])]});
            var Q13;
            Q13=makeQuery(id+"F1.opExtrude","SWEPT_EDGE",EDGE,{"disambiguationData":[OSD([sQuery(id+"F0.wireOp",EDGE,"E35.MirrorCS"),sQuery(id+"F0.wireOp",EDGE,"E45.MirrorCS")])]});
            var Q14;
            Q14=makeQuery(id+"F1.opExtrude","SWEPT_EDGE",EDGE,{"disambiguationData":[OSD([sQuery(id+"F0.wireOp",EDGE,"E38.MirrorCS"),sQuery(id+"F0.wireOp",EDGE,"E52.MirrorCS")])]});
            var Q15;
            Q15=makeQuery(id+"F1.opExtrude","SWEPT_EDGE",EDGE,{"disambiguationData":[OSD([sQuery(id+"F0.wireOp",EDGE,"E50.MirrorCS"),sQuery(id+"F0.wireOp",EDGE,"E53.MirrorCS")])]});
            var Q16;
            Q16=makeQuery(id+"F1.opExtrude","SWEPT_EDGE",EDGE,{"disambiguationData":[OSD([sQuery(id+"F0.wireOp",EDGE,"E50.MirrorCS"),sQuery(id+"F0.wireOp",EDGE,"E64.MirrorCS")])]});
            var Q17;
            Q17=makeQuery(id+"F1.opExtrude","SWEPT_EDGE",EDGE,{"disambiguationData":[OSD([sQuery(id+"F0.wireOp",EDGE,"E52.MirrorCS"),sQuery(id+"F0.wireOp",EDGE,"E57.MirrorCS")])]});
            var Q18;
            Q18=makeQuery(id+"F1.opExtrude","SWEPT_EDGE",EDGE,{"disambiguationData":[OSD([sQuery(id+"F0.wireOp",EDGE,"E35.MirrorCS"),sQuery(id+"F0.wireOp",EDGE,"E44.MirrorCS")])]});
            var Q19;
            Q19=makeQuery(id+"F1.opExtrude","SWEPT_EDGE",EDGE,{"disambiguationData":[OSD([sQuery(id+"F0.wireOp",EDGE,"E36.MirrorCS"),sQuery(id+"F0.wireOp",EDGE,"E46.MirrorCS")])]});
            var Q20;
            Q20=makeQuery(id+"F1.opExtrude","SWEPT_EDGE",EDGE,{"disambiguationData":[OSD([sQuery(id+"F0.wireOp",EDGE,"E34.MirrorCS"),sQuery(id+"F0.wireOp",EDGE,"E56.MirrorCS")])]});
            var Q21;
            Q21=makeQuery(id+"F1.opExtrude","SWEPT_EDGE",EDGE,{"disambiguationData":[OSD([sQuery(id+"F0.wireOp",EDGE,"E37.MirrorCS"),sQuery(id+"F0.wireOp",EDGE,"E40.MirrorCS")])]});
            var Q22;
            Q22=makeQuery(id+"F1.opExtrude","SWEPT_EDGE",EDGE,{"disambiguationData":[OSD([sQuery(id+"F0.wireOp",EDGE,"E59.MirrorCS"),sQuery(id+"F0.wireOp",EDGE,"E61.MirrorCS")])]});
            var Q23;
            Q23=makeQuery(id+"F1.opExtrude","SWEPT_EDGE",EDGE,{"disambiguationData":[OSD([sQuery(id+"F0.wireOp",EDGE,"E54.MirrorCS"),sQuery(id+"F0.wireOp",EDGE,"E63.MirrorCS")])]});
            var Q24;
            Q24=makeQuery(id+"F1.opExtrude","SWEPT_EDGE",EDGE,{"disambiguationData":[OSD([sQuery(id+"F0.wireOp",EDGE,"E3"),sQuery(id+"F0.wireOp",EDGE,"E4")])]});
            var Q25;
            Q25=makeQuery(id+"F1.opExtrude","SWEPT_EDGE",EDGE,{"disambiguationData":[OSD([sQuery(id+"F0.wireOp",EDGE,"E7"),sQuery(id+"F0.wireOp",EDGE,"E8")])]});
            var Q26;
            Q26=makeQuery(id+"F1.opExtrude","SWEPT_EDGE",EDGE,{"disambiguationData":[OSD([sQuery(id+"F0.wireOp",EDGE,"E11"),sQuery(id+"F0.wireOp",EDGE,"E12")])]});
            var Q27;
            Q27=makeQuery(id+"F1.opExtrude","SWEPT_EDGE",EDGE,{"disambiguationData":[OSD([sQuery(id+"F0.wireOp",EDGE,"E15"),sQuery(id+"F0.wireOp",EDGE,"E16")])]});
            var Q28;
            Q28=makeQuery(id+"F1.opExtrude","SWEPT_EDGE",EDGE,{"disambiguationData":[OSD([sQuery(id+"F0.wireOp",EDGE,"E19"),sQuery(id+"F0.wireOp",EDGE,"E20")])]});
            var Q29;
            Q29=makeQuery(id+"F1.opExtrude","SWEPT_EDGE",EDGE,{"disambiguationData":[OSD([sQuery(id+"F0.wireOp",EDGE,"E23"),sQuery(id+"F0.wireOp",EDGE,"E24")])]});
            var Q30;
            Q30=makeQuery(id+"F1.opExtrude","SWEPT_EDGE",EDGE,{"disambiguationData":[OSD([sQuery(id+"F0.wireOp",EDGE,"E27"),sQuery(id+"F0.wireOp",EDGE,"E28")])]});
            var Q31;
            Q31=makeQuery(id+"F1.opExtrude","SWEPT_EDGE",EDGE,{"disambiguationData":[OSD([sQuery(id+"F0.wireOp",EDGE,"E31"),sQuery(id+"F0.wireOp",EDGE,"E32")])]});
            var Q32;
            Q32=makeQuery(id+"F1.opExtrude","SWEPT_EDGE",EDGE,{"disambiguationData":[OSD([sQuery(id+"F0.wireOp",EDGE,"E75.MirrorCS"),sQuery(id+"F0.wireOp",EDGE,"E127.MirrorCS")])]});
            var Q33;
            Q33=makeQuery(id+"F1.opExtrude","SWEPT_EDGE",EDGE,{"disambiguationData":[OSD([sQuery(id+"F0.wireOp",EDGE,"E77.MirrorCS"),sQuery(id+"F0.wireOp",EDGE,"E101.MirrorCS")])]});
            var Q34;
            Q34=makeQuery(id+"F1.opExtrude","SWEPT_EDGE",EDGE,{"disambiguationData":[OSD([sQuery(id+"F0.wireOp",EDGE,"E72.MirrorCS"),sQuery(id+"F0.wireOp",EDGE,"E77.MirrorCS")])]});
            var Q35;
            Q35=makeQuery(id+"F1.opExtrude","SWEPT_EDGE",EDGE,{"disambiguationData":[OSD([sQuery(id+"F0.wireOp",EDGE,"E71.MirrorCS"),sQuery(id+"F0.wireOp",EDGE,"E116.MirrorCS")])]});
            var Q36;
            Q36=makeQuery(id+"F1.opExtrude","SWEPT_EDGE",EDGE,{"disambiguationData":[OSD([sQuery(id+"F0.wireOp",EDGE,"E71.MirrorCS"),sQuery(id+"F0.wireOp",EDGE,"E95.MirrorCS")])]});
            var Q37;
            Q37=makeQuery(id+"F1.opExtrude","SWEPT_EDGE",EDGE,{"disambiguationData":[OSD([sQuery(id+"F0.wireOp",EDGE,"E88.MirrorCS"),sQuery(id+"F0.wireOp",EDGE,"E110.MirrorCS")])]});
            var Q38;
            Q38=makeQuery(id+"F1.opExtrude","SWEPT_EDGE",EDGE,{"disambiguationData":[OSD([sQuery(id+"F0.wireOp",EDGE,"E68.MirrorCS"),sQuery(id+"F0.wireOp",EDGE,"E88.MirrorCS")])]});
            var Q39;
            Q39=makeQuery(id+"F1.opExtrude","SWEPT_EDGE",EDGE,{"disambiguationData":[OSD([sQuery(id+"F0.wireOp",EDGE,"E78.MirrorCS"),sQuery(id+"F0.wireOp",EDGE,"E104.MirrorCS")])]});
            var Q40;
            Q40=makeQuery(id+"F1.opExtrude","SWEPT_EDGE",EDGE,{"disambiguationData":[OSD([sQuery(id+"F0.wireOp",EDGE,"E69.MirrorCS"),sQuery(id+"F0.wireOp",EDGE,"E78.MirrorCS")])]});
            var Q41;
            Q41=makeQuery(id+"F1.opExtrude","SWEPT_EDGE",EDGE,{"disambiguationData":[OSD([sQuery(id+"F0.wireOp",EDGE,"E65.MirrorCS"),sQuery(id+"F0.wireOp",EDGE,"E100.MirrorCS")])]});
            var Q42;
            Q42=makeQuery(id+"F1.opExtrude","SWEPT_EDGE",EDGE,{"disambiguationData":[OSD([sQuery(id+"F0.wireOp",EDGE,"E65.MirrorCS"),sQuery(id+"F0.wireOp",EDGE,"E66.MirrorCS")])]});
            var Q43;
            Q43=makeQuery(id+"F1.opExtrude","SWEPT_EDGE",EDGE,{"disambiguationData":[OSD([sQuery(id+"F0.wireOp",EDGE,"E93.MirrorCS"),sQuery(id+"F0.wireOp",EDGE,"E111.MirrorCS")])]});
            var Q44;
            Q44=makeQuery(id+"F1.opExtrude","SWEPT_EDGE",EDGE,{"disambiguationData":[OSD([sQuery(id+"F0.wireOp",EDGE,"E74.MirrorCS"),sQuery(id+"F0.wireOp",EDGE,"E93.MirrorCS")])]});
            var Q45;
            Q45=makeQuery(id+"F1.opExtrude","SWEPT_EDGE",EDGE,{"disambiguationData":[OSD([sQuery(id+"F0.wireOp",EDGE,"E87.MirrorCS"),sQuery(id+"F0.wireOp",EDGE,"E114.MirrorCS")])]});
            var Q46;
            Q46=makeQuery(id+"F1.opExtrude","SWEPT_EDGE",EDGE,{"disambiguationData":[OSD([sQuery(id+"F0.wireOp",EDGE,"E84.MirrorCS"),sQuery(id+"F0.wireOp",EDGE,"E87.MirrorCS")])]});
            var Q47;
            Q47=makeQuery(id+"F1.opExtrude","SWEPT_EDGE",EDGE,{"disambiguationData":[OSD([sQuery(id+"F0.wireOp",EDGE,"E70.MirrorCS"),sQuery(id+"F0.wireOp",EDGE,"E97.MirrorCS")])]});
            var Q48;
            Q48=makeQuery(id+"F1.opExtrude","SWEPT_EDGE",EDGE,{"disambiguationData":[OSD([sQuery(id+"F0.wireOp",EDGE,"E70.MirrorCS"),sQuery(id+"F0.wireOp",EDGE,"E117.MirrorCS")])]});
            var Q49;
            Q49=makeQuery(id+"F1.opExtrude","SWEPT_EDGE",EDGE,{"disambiguationData":[OSD([sQuery(id+"F0.wireOp",EDGE,"E81.MirrorCS"),sQuery(id+"F0.wireOp",EDGE,"E86.MirrorCS")])]});
            var Q50;
            Q50=makeQuery(id+"F1.opExtrude","SWEPT_EDGE",EDGE,{"disambiguationData":[OSD([sQuery(id+"F0.wireOp",EDGE,"E86.MirrorCS"),sQuery(id+"F0.wireOp",EDGE,"E119.MirrorCS")])]});
            var Q51;
            Q51=makeQuery(id+"F1.opExtrude","SWEPT_EDGE",EDGE,{"disambiguationData":[OSD([sQuery(id+"F0.wireOp",EDGE,"E67.MirrorCS"),sQuery(id+"F0.wireOp",EDGE,"E90.MirrorCS")])]});
            var Q52;
            Q52=makeQuery(id+"F1.opExtrude","SWEPT_EDGE",EDGE,{"disambiguationData":[OSD([sQuery(id+"F0.wireOp",EDGE,"E90.MirrorCS"),sQuery(id+"F0.wireOp",EDGE,"E121.MirrorCS")])]});
            var Q53;
            Q53=makeQuery(id+"F1.opExtrude","SWEPT_EDGE",EDGE,{"disambiguationData":[OSD([sQuery(id+"F0.wireOp",EDGE,"E85.MirrorCS"),sQuery(id+"F0.wireOp",EDGE,"E91.MirrorCS")])]});
            var Q54;
            Q54=makeQuery(id+"F1.opExtrude","SWEPT_EDGE",EDGE,{"disambiguationData":[OSD([sQuery(id+"F0.wireOp",EDGE,"E85.MirrorCS"),sQuery(id+"F0.wireOp",EDGE,"E120.MirrorCS")])]});
            var Q55;
            Q55=makeQuery(id+"F1.opExtrude","SWEPT_EDGE",EDGE,{"disambiguationData":[OSD([sQuery(id+"F0.wireOp",EDGE,"E82.MirrorCS"),sQuery(id+"F0.wireOp",EDGE,"E94.MirrorCS")])]});
            var Q56;
            Q56=makeQuery(id+"F1.opExtrude","SWEPT_EDGE",EDGE,{"disambiguationData":[OSD([sQuery(id+"F0.wireOp",EDGE,"E94.MirrorCS"),sQuery(id+"F0.wireOp",EDGE,"E98.MirrorCS")])]});
            var Q57;
            Q57=makeQuery(id+"F1.opExtrude","SWEPT_EDGE",EDGE,{"disambiguationData":[OSD([sQuery(id+"F0.wireOp",EDGE,"E76.MirrorCS"),sQuery(id+"F0.wireOp",EDGE,"E92.MirrorCS")])]});
            var Q58;
            Q58=makeQuery(id+"F1.opExtrude","SWEPT_EDGE",EDGE,{"disambiguationData":[OSD([sQuery(id+"F0.wireOp",EDGE,"E76.MirrorCS"),sQuery(id+"F0.wireOp",EDGE,"E107.MirrorCS")])]});
            var Q59;
            Q59=makeQuery(id+"F1.opExtrude","SWEPT_EDGE",EDGE,{"disambiguationData":[OSD([sQuery(id+"F0.wireOp",EDGE,"E79.MirrorCS"),sQuery(id+"F0.wireOp",EDGE,"E89.MirrorCS")])]});
            var Q60;
            Q60=makeQuery(id+"F1.opExtrude","SWEPT_EDGE",EDGE,{"disambiguationData":[OSD([sQuery(id+"F0.wireOp",EDGE,"E89.MirrorCS"),sQuery(id+"F0.wireOp",EDGE,"E112.MirrorCS")])]});
            var Q61;
            Q61=makeQuery(id+"F1.opExtrude","SWEPT_EDGE",EDGE,{"disambiguationData":[OSD([sQuery(id+"F0.wireOp",EDGE,"E73.MirrorCS"),sQuery(id+"F0.wireOp",EDGE,"E80.MirrorCS")])]});
            var Q62;
            Q62=makeQuery(id+"F1.opExtrude","SWEPT_EDGE",EDGE,{"disambiguationData":[OSD([sQuery(id+"F0.wireOp",EDGE,"E80.MirrorCS"),sQuery(id+"F0.wireOp",EDGE,"E126.MirrorCS")])]});
            var Q63;
            Q63=makeQuery(id+"F1.opExtrude","SWEPT_EDGE",EDGE,{"disambiguationData":[OSD([sQuery(id+"F0.wireOp",EDGE,"E75.MirrorCS"),sQuery(id+"F0.wireOp",EDGE,"E83.MirrorCS")])]});
            fillet(context, id + "F3", {"entities" : qUnion([Q0, Q1, Q2, Q3, Q4, Q5, Q6, Q7, Q8, Q9, Q10, Q11, Q12, Q13, Q14, Q15, Q16, Q17, Q18, Q19, Q20, Q21, Q22, Q23, Q24, Q25, Q26, Q27, Q28, Q29, Q30, Q31, Q32, Q33, Q34, Q35, Q36, Q37, Q38, Q39, Q40, Q41, Q42, Q43, Q44, Q45, Q46, Q47, Q48, Q49, Q50, Q51, Q52, Q53, Q54, Q55, Q56, Q57, Q58, Q59, Q60, Q61, Q62, Q63]), "radius" : 1 * mm, "tangentPropagation" : true, "allowEdgeOverflow" : false});
        }
        {
            var Q0;
            Q0=makeQuery(id+"F1.opExtrude","SWEPT_EDGE",EDGE,{"disambiguationData":[OSD([sQuery(id+"F0.wireOp",EDGE,"E132"),sQuery(id+"F0.wireOp",EDGE,"E134.MirrorCS")])]});
            var Q1;
            Q1=makeQuery(id+"F1.opExtrude","SWEPT_EDGE",EDGE,{"disambiguationData":[OSD([sQuery(id+"F0.wireOp",EDGE,"E133.MirrorCS"),sQuery(id+"F0.wireOp",EDGE,"E135.MirrorCS")])]});
            var Q2;
            Q2=makeQuery(id+"F1.opExtrude","SWEPT_EDGE",EDGE,{"disambiguationData":[OSD([sQuery(id+"F0.wireOp",EDGE,"E133.MirrorCS"),sQuery(id+"F0.wireOp",EDGE,"E137.MirrorCS")])]});
            var Q3;
            Q3=makeQuery(id+"F1.opExtrude","SWEPT_EDGE",EDGE,{"disambiguationData":[OSD([sQuery(id+"F0.wireOp",EDGE,"E132"),sQuery(id+"F0.wireOp",EDGE,"E136")])]});
            var Q4;
            Q4=makeQuery(id+"F1.opExtrude","SWEPT_EDGE",EDGE,{"disambiguationData":[OSD([sQuery(id+"F0.wireOp",EDGE,"E134.MirrorCS"),sQuery(id+"F0.wireOp",EDGE,"E136")])]});
            var Q5;
            Q5=makeQuery(id+"F1.opExtrude","SWEPT_EDGE",EDGE,{"disambiguationData":[OSD([sQuery(id+"F0.wireOp",EDGE,"E135.MirrorCS"),sQuery(id+"F0.wireOp",EDGE,"E137.MirrorCS")])]});
            fillet(context, id + "F4", {"entities" : qUnion([Q0, Q1, Q2, Q3, Q4, Q5]), "radius" : 5 * mm, "tangentPropagation" : true, "allowEdgeOverflow" : false});
        }
        {
            var Q0;
            Q0=makeQuery(id+"F1.opExtrude","CAP_EDGE",EDGE,{"disambiguationData":[OSD([sQuery(id+"F0.wireOp",EDGE,"E57.MirrorCS")])],"isStart":false});
            var Q1;
            Q1=makeQuery(id+"F1.opExtrude","CAP_EDGE",EDGE,{"disambiguationData":[OSD([sQuery(id+"F0.wireOp",EDGE,"E57.MirrorCS")])],"isStart":true});
            chamfer(context, id + "F5", {"entities" : qUnion([Q0, Q1]), "width" : 0.5 * mm, "tangentPropagation" : true});
        }
    });
